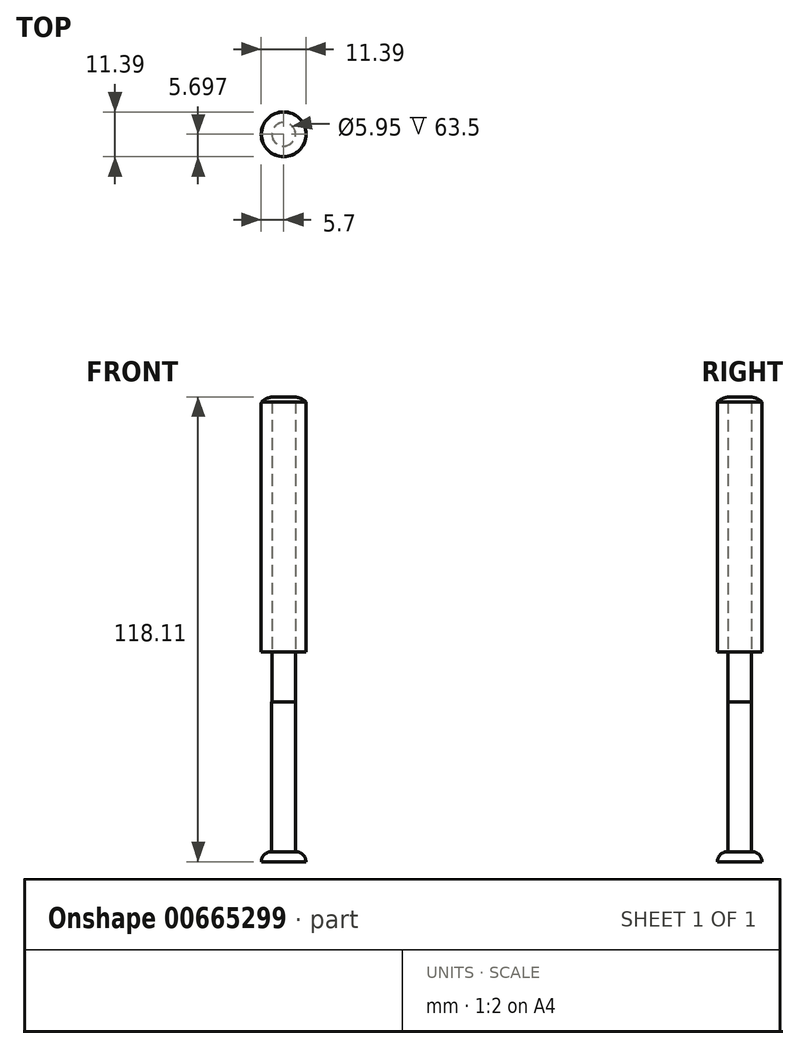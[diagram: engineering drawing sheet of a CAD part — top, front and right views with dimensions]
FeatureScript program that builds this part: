
annotation { "Feature Type Name" : "Feature", "Feature Type Description" : "" }
export const myFeature = defineFeature(function(context is Context, id is Id, definition is map)
    precondition{}
    {
        {
            var Q0;
            Q0=qCreatedBy(makeId("Top.planeOp"),FACE);
            var sketch = newSketch(context, id + "F0", { "sketchPlane" : qUnion([Q0])});
            skCircle(sketch, "E0", {"center": v(-59.88, -50.47) * mm, "radius": 5.66 * mm});
            skSolve(sketch);
        }
        {
            var Q0;
            Q0=makeQuery(id+"F0.imprint","IMPRINT",FACE,{"disambiguationData":[TD([[makeQuery(id+"F0.imprint","IMPRINT",EDGE,{"derivedFrom":sQuery(id+"F0.wireOp",EDGE,"E0")}),1.0]])]});
            extrude(context, id + "F1", {"entities" : qUnion([Q0]), "depth" : 2.54 * mm, "offsetDistance" : 25.4 * mm});
        }
        {
            var Q0;
            Q0=makeQuery(id+"F1.opExtrude","CAP_EDGE",EDGE,{"disambiguationData":[OSD([sQuery(id+"F0.wireOp",EDGE,"E0")])],"isStart":false});
            fillet(context, id + "F2", {"entities" : qUnion([Q0]), "radius" : 2.54 * mm, "tangentPropagation" : true, "allowEdgeOverflow" : false});
        }
        {
            var Q0;
            Q0=makeQuery(id+"F1.opExtrude","CAP_FACE",FACE,{"disambiguationData":[OSD([sQuery(id+"F0.wireOp",EDGE,"E0")])],"isStart":false});
            var sketch = newSketch(context, id + "F3", { "sketchPlane" : qUnion([Q0])});
            skCircle(sketch, "E1", {"center": v(-59.88, -50.47) * mm, "radius": 3.02 * mm});
            skSolve(sketch);
        }
        {
            var Q0;
            Q0=makeQuery(id+"F3.imprint","IMPRINT",FACE,{"disambiguationData":[TD([[makeQuery(id+"F3.imprint","IMPRINT",EDGE,{"derivedFrom":sQuery(id+"F3.wireOp",EDGE,"E1")}),1.0]])]});
            extrude(context, id + "F4", {"entities" : qUnion([Q0]), "operationType" : NewBodyOperationType.ADD, "depth" : 38.1 * mm, "offsetDistance" : 25.4 * mm});
        }
        {
            var Q0;
            Q0=makeQuery(id+"F4.opExtrude","CAP_FACE",FACE,{"disambiguationData":[OSD([sQuery(id+"F3.wireOp",EDGE,"E1")])],"isStart":false});
            var sketch = newSketch(context, id + "F5", { "sketchPlane" : qUnion([Q0])});
            skCircle(sketch, "E2", {"center": v(-59.88, -50.47) * mm, "radius": 2.97 * mm});
            skSolve(sketch);
        }
        {
            var Q0;
            Q0=makeQuery(id+"F5.imprint","IMPRINT",FACE,{"disambiguationData":[TD([[makeQuery(id+"F5.imprint","IMPRINT",EDGE,{"derivedFrom":sQuery(id+"F5.wireOp",EDGE,"E2")}),1.0]])]});
            extrude(context, id + "F6", {"entities" : qUnion([Q0]), "operationType" : NewBodyOperationType.ADD, "depth" : 12.7 * mm, "offsetDistance" : 25.4 * mm});
        }
        {
            var Q0;
            Q0=makeQuery(id+"F6.opExtrude","CAP_FACE",FACE,{"disambiguationData":[OSD([sQuery(id+"F5.wireOp",EDGE,"E2")])],"isStart":false});
            var sketch = newSketch(context, id + "F7", { "sketchPlane" : qUnion([Q0])});
            skCircle(sketch, "E3", {"center": v(-59.88, -50.47) * mm, "radius": 5.7 * mm});
            skSolve(sketch);
        }
        {
            var Q0;
            Q0=makeQuery(id+"F7.imprint","IMPRINT",FACE,{"disambiguationData":[TD([[makeQuery(id+"F7.imprint","IMPRINT",EDGE,{"derivedFrom":sQuery(id+"F7.wireOp",EDGE,"E3")}),1.0]])]});
            extrude(context, id + "F8", {"entities" : qUnion([Q0]), "depth" : 63.5 * mm, "offsetDistance" : 25.4 * mm});
        }
        {
            var Q0;
            Q0=makeQuery(id+"F8.opExtrude","CAP_EDGE",EDGE,{"disambiguationData":[OSD([sQuery(id+"F7.wireOp",EDGE,"E3")])],"isStart":true});
            var Q1;
            Q1=makeQuery(id+"F4.opExtrude","CAP_EDGE",EDGE,{"disambiguationData":[OSD([sQuery(id+"F3.wireOp",EDGE,"E1")])],"isStart":false});
            loft(context, id + "F9", {"bodyType" : ToolBodyType.SURFACE, "wireProfilesArray" : [{ "wireProfileEntities" : qUnion([Q0]) }, { "wireProfileEntities" : qUnion([Q1]) }]});
        }
        {
            var Q0;
            Q0=makeQuery(id+"F8.opExtrude","CAP_FACE",FACE,{"disambiguationData":[OSD([sQuery(id+"F5.wireOp",EDGE,"E2"),sQuery(id+"F7.wireOp",EDGE,"E3")])],"isStart":false});
            var sketch = newSketch(context, id + "F10", { "sketchPlane" : qUnion([Q0])});
            skCircle(sketch, "E4", {"center": v(-59.88, -50.47) * mm, "radius": 5.66 * mm});
            skSolve(sketch);
        }
        {
            var Q0;
            Q0 = qSketchRegion(id + "F10", true);
            extrude(context, id + "F11", {"entities" : qUnion([Q0]), "operationType" : NewBodyOperationType.ADD, "depth" : 1.27 * mm, "offsetDistance" : 25.4 * mm});
        }
        {
            var Q0;
            Q0=makeQuery(id+"F11.opExtrude","CAP_EDGE",EDGE,{"disambiguationData":[OSD([sQuery(id+"F10.wireOp",EDGE,"E4")])],"isStart":false});
            var Q1;
            Q1=makeQuery(id+"F8.opExtrude","CAP_EDGE",EDGE,{"disambiguationData":[OSD([sQuery(id+"F7.wireOp",EDGE,"E3")])],"isStart":false});
            fillet(context, id + "F12", {"entities" : qUnion([Q0, Q1]), "radius" : 5.08 * mm, "tangentPropagation" : true, "allowEdgeOverflow" : false});
        }
        {
            var Q0;
            Q0=makeQuery(id+"F8.opExtrude","SWEPT_FACE",FACE,{"disambiguationData":[OSD([sQuery(id+"F7.wireOp",EDGE,"E3")])]});
            cPlane(context, id + "F13", {"entities" : qUnion([Q0]), "cplaneType" : CPlaneType.LINE_ANGLE, "offset" : 25.4 * mm, "angle" : 360 * degree, "width" : 152.4 * mm, "height" : 152.4 * mm});
        }
    });
